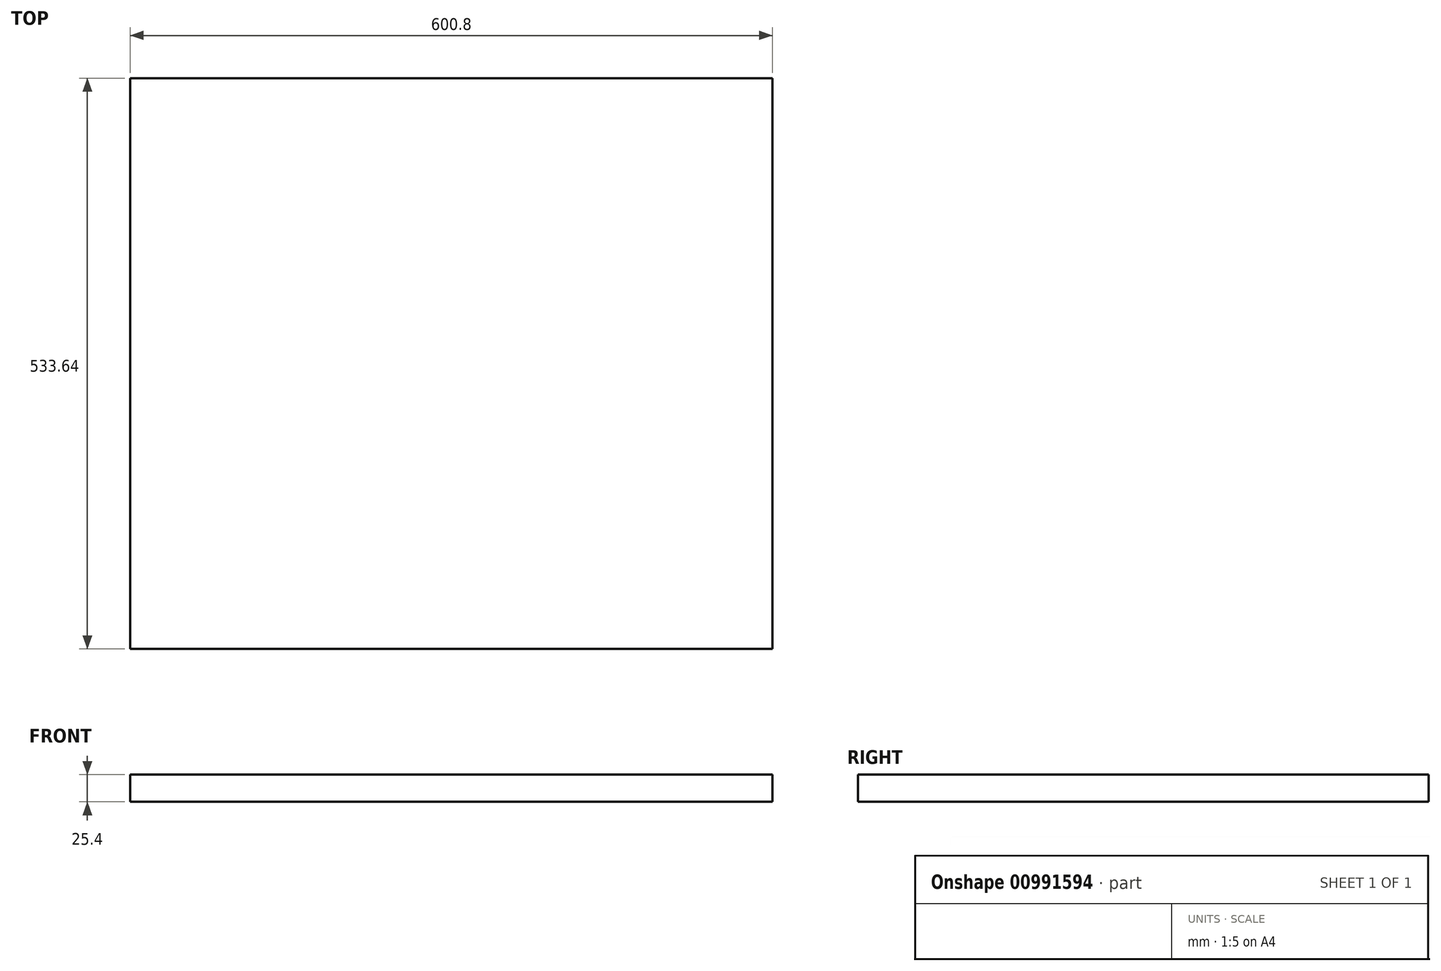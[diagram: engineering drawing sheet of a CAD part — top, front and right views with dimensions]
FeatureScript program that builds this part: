
annotation { "Feature Type Name" : "Feature", "Feature Type Description" : "" }
export const myFeature = defineFeature(function(context is Context, id is Id, definition is map)
    precondition{}
    {
        {
            var Q0;
            Q0=qCreatedBy(makeId("Top.planeOp"),FACE);
            var sketch = newSketch(context, id + "F0", { "sketchPlane" : qUnion([Q0])});
            skLineSegment(sketch, "E0.bottom", {"start": v(-300.4, 266.82) * mm, "end": v(300.4, 266.82) * mm});
            skLineSegment(sketch, "E0.top", {"start": v(-300.4, -266.82) * mm, "end": v(300.4, -266.82) * mm});
            skLineSegment(sketch, "E0.left", {"start": v(-300.4, 266.82) * mm, "end": v(-300.4, -266.82) * mm});
            skLineSegment(sketch, "E0.right", {"start": v(300.4, 266.82) * mm, "end": v(300.4, -266.82) * mm});
            skPoint(sketch, "E0.middle", {"position": v(0, 0) * mm});
            skSolve(sketch);
        }
        {
            var Q0;
            Q0=makeQuery(id+"F0.imprint","IMPRINT",FACE,{"disambiguationData":[TD([[makeQuery(id+"F0.imprint","IMPRINT",EDGE,{"derivedFrom":sQuery(id+"F0.wireOp",EDGE,"E0.bottom")}),-1.0]])]});
            extrude(context, id + "F1", {"entities" : qUnion([Q0]), "depth" : 25.4 * mm, "offsetDistance" : 25.4 * mm});
        }
    });
